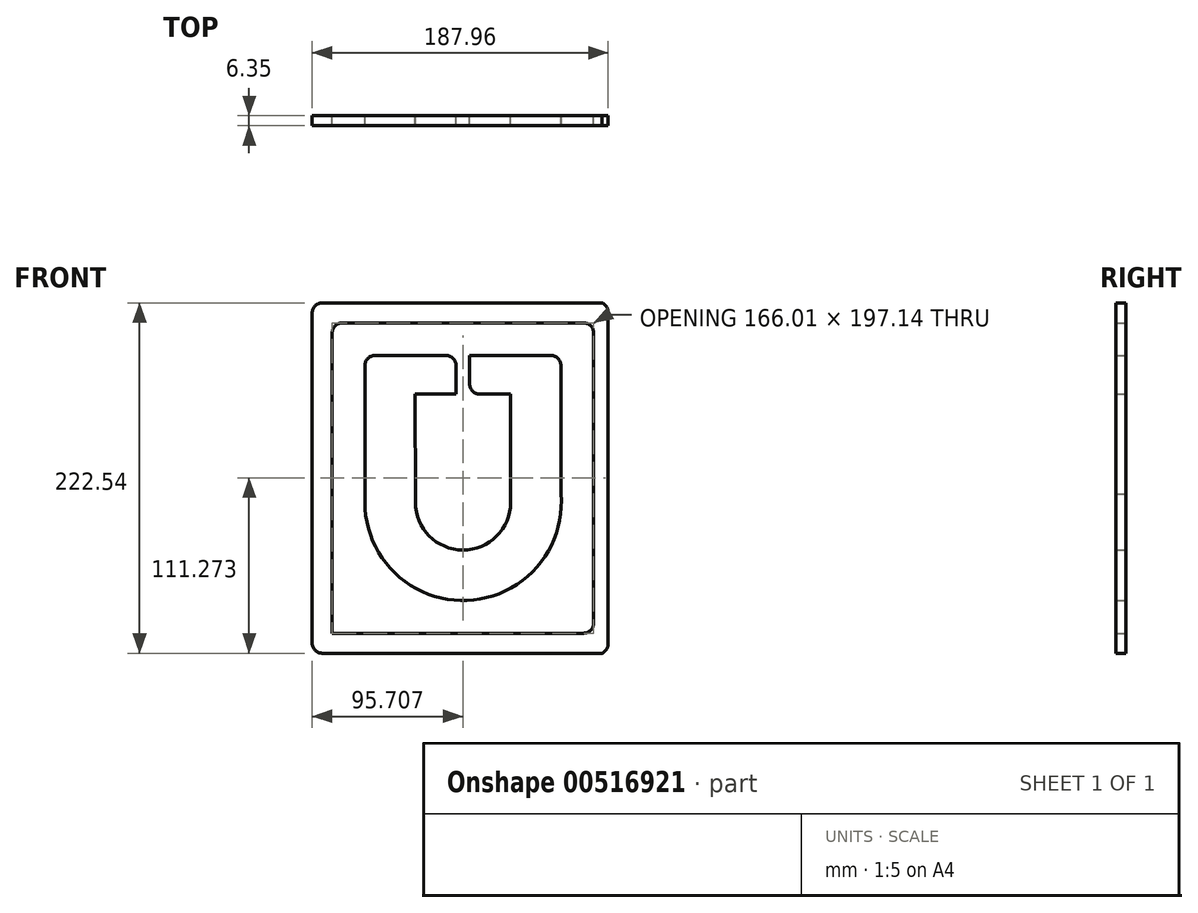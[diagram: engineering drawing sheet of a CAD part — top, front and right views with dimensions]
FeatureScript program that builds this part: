
annotation { "Feature Type Name" : "Feature", "Feature Type Description" : "" }
export const myFeature = defineFeature(function(context is Context, id is Id, definition is map)
    precondition{}
    {
        {
            var Q0;
            Q0=qCreatedBy(makeId("Front.planeOp"),FACE);
            var sketch = newSketch(context, id + "F0", { "sketchPlane" : qUnion([Q0])});
            skLineSegment(sketch, "E0.bottom", {"start": v(96.66, 108.78) * mm, "end": v(45.08, 108.78) * mm});
            skLineSegment(sketch, "E0.top", {"start": v(71.14, 84.27) * mm, "end": v(51.43, 84.27) * mm});
            skLineSegment(sketch, "E1.left", {"start": v(36.4, 102.43) * mm, "end": v(36.4, 84.27) * mm});
            skLineSegment(sketch, "E1.right", {"start": v(45.08, 108.78) * mm, "end": v(45.08, 90.62) * mm});
            skLineSegment(sketch, "E2.trimOffspring", {"start": v(30.05, 108.78) * mm, "end": v(-15.15, 108.78) * mm});
            skLineSegment(sketch, "E3.trimOffspring", {"start": v(36.4, 84.27) * mm, "end": v(10.5, 84.27) * mm});
            skLineSegment(sketch, "E4", {"start": v(71.14, 84.27) * mm, "end": v(71.14, 15.4) * mm});
            skLineSegment(sketch, "E5", {"start": v(10.5, 84.27) * mm, "end": v(10.59, 15.63) * mm});
            skArc(sketch, "E6", {"start": v(10.59, 15.63) * mm, "mid": v(40.75, -14.76) * mm, "end": v(71.14, 15.4) * mm});
            skArc(sketch, "E7", {"start": v(-21.5, 15.7) * mm, "mid": v(43.43, -46.8) * mm, "end": v(103, 20.83) * mm});
            skLineSegment(sketch, "E8.bottom", {"start": v(117.4, 129.53) * mm, "end": v(-35.92, 129.53) * mm});
            skLineSegment(sketch, "E8.top", {"start": v(117.4, -67.6) * mm, "end": v(-42.27, -67.6) * mm});
            skLineSegment(sketch, "E8.left", {"start": v(123.74, 123.18) * mm, "end": v(123.74, -61.26) * mm});
            skLineSegment(sketch, "E8.right", {"start": v(-42.27, 123.18) * mm, "end": v(-42.27, -67.6) * mm});
            skLineSegment(sketch, "E9.left", {"start": v(-54.97, 135.88) * mm, "end": v(-54.97, -73.96) * mm});
            skLineSegment(sketch, "E9.right", {"start": v(133, 136.41) * mm, "end": v(133, -74.49) * mm});
            skLineSegment(sketch, "E10", {"start": v(103, 20.83) * mm, "end": v(103, 102.43) * mm});
            skLineSegment(sketch, "E11", {"start": v(-21.5, 102.43) * mm, "end": v(-21.5, 15.7) * mm});
            skPoint(sketch, "E12.visualSharp", {"position": v(36.4, 108.78) * mm});
            skArc(sketch, "E12.filletArc", {"start": v(36.4, 102.43) * mm, "mid": v(34.54, 106.92) * mm, "end": v(30.05, 108.78) * mm});
            skPoint(sketch, "E13.visualSharp", {"position": v(45.08, 84.27) * mm});
            skArc(sketch, "E13.filletArc", {"start": v(45.08, 90.62) * mm, "mid": v(46.94, 86.13) * mm, "end": v(51.43, 84.27) * mm});
            skPoint(sketch, "E14.visualSharp", {"position": v(103, 108.78) * mm});
            skArc(sketch, "E14.filletArc", {"start": v(103, 102.43) * mm, "mid": v(101.15, 106.92) * mm, "end": v(96.66, 108.78) * mm});
            skPoint(sketch, "E15.visualSharp", {"position": v(-21.5, 108.78) * mm});
            skArc(sketch, "E15.filletArc", {"start": v(-15.15, 108.78) * mm, "mid": v(-19.64, 106.92) * mm, "end": v(-21.5, 102.43) * mm});
            skArc(sketch, "E16.filletArc", {"start": v(-48.62, 142.23) * mm, "mid": v(-53.1, 140.37) * mm, "end": v(-54.97, 135.88) * mm});
            skPoint(sketch, "E17.visualSharp", {"position": v(-42.27, 129.53) * mm});
            skArc(sketch, "E17.filletArc", {"start": v(-35.92, 129.53) * mm, "mid": v(-40.4, 127.67) * mm, "end": v(-42.27, 123.18) * mm});
            skArc(sketch, "E18.filletArc", {"start": v(133, 136.41) * mm, "mid": v(131.95, 139.9) * mm, "end": v(129.18, 142.23) * mm});
            skPoint(sketch, "E19.visualSharp", {"position": v(123.74, 129.53) * mm});
            skArc(sketch, "E19.filletArc", {"start": v(123.74, 123.18) * mm, "mid": v(121.88, 127.67) * mm, "end": v(117.4, 129.53) * mm});
            skPoint(sketch, "E20.visualSharp", {"position": v(123.74, -67.6) * mm});
            skArc(sketch, "E20.filletArc", {"start": v(117.4, -67.6) * mm, "mid": v(121.88, -65.75) * mm, "end": v(123.74, -61.26) * mm});
            skPoint(sketch, "E21.visualSharp", {"position": v(133, -80.3) * mm});
            skArc(sketch, "E21.filletArc", {"start": v(129.18, -80.3) * mm, "mid": v(131.95, -77.97) * mm, "end": v(133, -74.49) * mm});
            skArc(sketch, "E22.filletArc", {"start": v(-54.97, -73.96) * mm, "mid": v(-53.1, -78.45) * mm, "end": v(-48.62, -80.3) * mm});
            skLineSegment(sketch, "E23", {"start": v(-48.62, -80.3) * mm, "end": v(129.18, -80.3) * mm});
            skLineSegment(sketch, "E24", {"start": v(-67.67, 129.53) * mm, "end": v(-67.67, 154.93) * mm});
            skLineSegment(sketch, "E25.bottom", {"start": v(-67.67, 154.93) * mm, "end": v(14.88, 154.93) * mm});
            skLineSegment(sketch, "E25.top", {"start": v(-67.67, -92.72) * mm, "end": v(14.88, -92.72) * mm});
            skLineSegment(sketch, "E25.left", {"start": v(-67.67, 154.93) * mm, "end": v(-67.67, -92.72) * mm});
            skLineSegment(sketch, "E25.right", {"start": v(148.23, 154.93) * mm, "end": v(148.23, -92.72) * mm});
            skLineSegment(sketch, "E26", {"start": v(-48.62, 142.23) * mm, "end": v(129.18, 142.23) * mm});
            skArc(sketch, "E27", {"start": v(65.68, 154.93) * mm, "mid": v(40.28, 180.33) * mm, "end": v(14.88, 154.93) * mm});
            skCircle(sketch, "E28", {"center": v(40.28, 154.93) * mm, "radius": 6.35 * mm});
            skLineSegment(sketch, "E29.trimOffspring", {"start": v(65.68, 154.93) * mm, "end": v(148.23, 154.93) * mm});
            skCircle(sketch, "E30", {"center": v(40.28, -92.72) * mm, "radius": 6.35 * mm});
            skArc(sketch, "E31.trimOffspring", {"start": v(14.88, -92.72) * mm, "mid": v(40.28, -118.12) * mm, "end": v(65.68, -92.72) * mm});
            skLineSegment(sketch, "E32.trimOffspring", {"start": v(65.68, -92.72) * mm, "end": v(148.23, -92.72) * mm});
            skSolve(sketch);
        }
        {
            var Q0;
            Q0=makeQuery(id+"F0.imprint","IMPRINT",FACE,{"disambiguationData":[TD([[makeQuery(id+"F0.imprint","IMPRINT",EDGE,{"derivedFrom":sQuery(id+"F0.wireOp",EDGE,"E0.bottom")}),1.0]])]});
            extrude(context, id + "F1", {"entities" : qUnion([Q0]), "depth" : 6.35 * mm, "offsetDistance" : 25.4 * mm});
        }
        {
            var Q0;
            Q0=makeQuery(id+"F0.imprint","IMPRINT",FACE,{"disambiguationData":[TD([[makeQuery(id+"F0.imprint","IMPRINT",EDGE,{"derivedFrom":sQuery(id+"F0.wireOp",EDGE,"E8.bottom")}),-1.0]])]});
            extrude(context, id + "F2", {"entities" : qUnion([Q0]), "depth" : 6.35 * mm, "offsetDistance" : 25.4 * mm});
        }
    });
